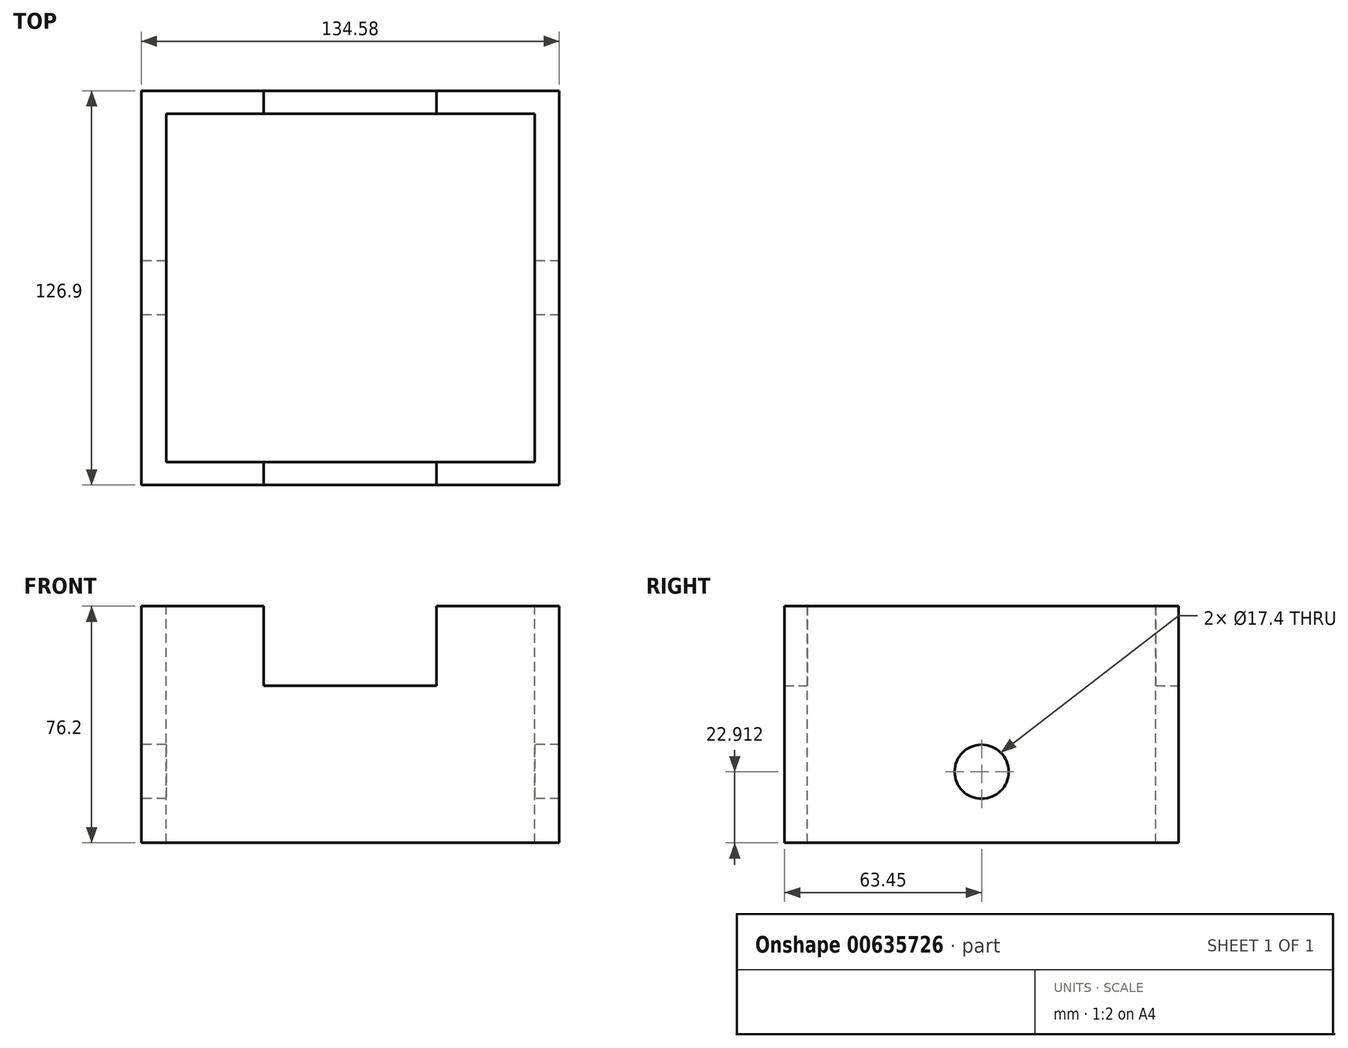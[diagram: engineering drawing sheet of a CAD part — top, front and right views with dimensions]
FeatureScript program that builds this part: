
annotation { "Feature Type Name" : "Feature", "Feature Type Description" : "" }
export const myFeature = defineFeature(function(context is Context, id is Id, definition is map)
    precondition{}
    {
        {
            var Q0;
            Q0=qCreatedBy(makeId("Top.planeOp"),FACE);
            var sketch = newSketch(context, id + "F0", { "sketchPlane" : qUnion([Q0])});
            skLineSegment(sketch, "E0.bottom", {"start": v(-67.29, 63.45) * mm, "end": v(67.29, 63.45) * mm});
            skLineSegment(sketch, "E0.top", {"start": v(-67.29, -63.45) * mm, "end": v(67.29, -63.45) * mm});
            skLineSegment(sketch, "E0.left", {"start": v(-67.29, 63.45) * mm, "end": v(-67.29, -63.45) * mm});
            skLineSegment(sketch, "E0.right", {"start": v(67.29, 63.45) * mm, "end": v(67.29, -63.45) * mm});
            skPoint(sketch, "E0.middle", {"position": v(0, 0) * mm});
            skLineSegment(sketch, "E1.bottom", {"start": v(-60.06, 53.2) * mm, "end": v(60.06, 53.2) * mm});
            skLineSegment(sketch, "E1.top", {"start": v(-60.06, -53.2) * mm, "end": v(60.06, -53.2) * mm});
            skLineSegment(sketch, "E1.left", {"start": v(-60.06, 53.2) * mm, "end": v(-60.06, -53.2) * mm});
            skLineSegment(sketch, "E1.right", {"start": v(60.06, 53.2) * mm, "end": v(60.06, -53.2) * mm});
            skSolve(sketch);
        }
        {
            var Q0;
            Q0=makeQuery(id+"F0.imprint","IMPRINT",FACE,{"disambiguationData":[TD([[makeQuery(id+"F0.imprint","IMPRINT",EDGE,{"derivedFrom":sQuery(id+"F0.wireOp",EDGE,"E1.bottom")}),-1.0]])]});
            var Q1;
            Q1=makeQuery(id+"F0.imprint","IMPRINT",FACE,{"disambiguationData":[TD([[makeQuery(id+"F0.imprint","IMPRINT",EDGE,{"derivedFrom":sQuery(id+"F0.wireOp",EDGE,"E0.bottom")}),-1.0]])]});
            extrude(context, id + "F1", {"entities" : qUnion([Q0, Q1]), "depth" : 50.8 * mm, "offsetDistance" : 25.4 * mm});
        }
        {
            var Q0;
            Q0=makeQuery(id+"F1.opExtrude","SWEPT_FACE",FACE,{"disambiguationData":[OSD([sQuery(id+"F0.wireOp",EDGE,"E0.left")])]});
            var sketch = newSketch(context, id + "F2", { "sketchPlane" : qUnion([Q0])});
            skCircle(sketch, "E2", {"center": v(0, 22.91) * mm, "radius": 8.7 * mm});
            skSolve(sketch);
        }
        {
            var Q0;
            Q0=makeQuery(id+"F2.imprint","IMPRINT",FACE,{"disambiguationData":[TD([[makeQuery(id+"F2.imprint","IMPRINT",EDGE,{"derivedFrom":sQuery(id+"F2.wireOp",EDGE,"E2")}),1.0]])]});
            extrude(context, id + "F3", {"entities" : qUnion([Q0]), "operationType" : NewBodyOperationType.REMOVE, "oppositeDirection" : true, "depth" : 508 * mm, "offsetDistance" : 25.4 * mm});
        }
        {
            var Q0;
            Q0=makeQuery(id+"F1.opExtrude","CAP_FACE",FACE,{"disambiguationData":[OSD([sQuery(id+"F0.wireOp",EDGE,"E0.bottom"),sQuery(id+"F0.wireOp",EDGE,"E0.top"),sQuery(id+"F0.wireOp",EDGE,"E0.left"),sQuery(id+"F0.wireOp",EDGE,"E0.right")])],"isStart":false});
            extrude(context, id + "F4", {"entities" : qUnion([Q0]), "operationType" : NewBodyOperationType.ADD, "depth" : 25.4 * mm, "offsetDistance" : 25.4 * mm});
        }
        {
            var Q0;
            Q0=makeQuery(id+"F4.opExtrude","CAP_FACE",FACE,{"disambiguationData":[OSD([sQuery(id+"F0.wireOp",EDGE,"E0.bottom"),sQuery(id+"F0.wireOp",EDGE,"E0.top"),sQuery(id+"F0.wireOp",EDGE,"E0.left"),sQuery(id+"F0.wireOp",EDGE,"E0.right")])],"isStart":false});
            var sketch = newSketch(context, id + "F5", { "sketchPlane" : qUnion([Q0])});
            skLineSegment(sketch, "E3.bottom", {"start": v(-59.3, 56.09) * mm, "end": v(59.3, 56.09) * mm});
            skLineSegment(sketch, "E3.top", {"start": v(-59.3, -56.09) * mm, "end": v(59.3, -56.09) * mm});
            skLineSegment(sketch, "E3.left", {"start": v(-59.3, 56.09) * mm, "end": v(-59.3, -56.09) * mm});
            skLineSegment(sketch, "E3.right", {"start": v(59.3, 56.09) * mm, "end": v(59.3, -56.09) * mm});
            skPoint(sketch, "E3.middle", {"position": v(0, 0) * mm});
            skSolve(sketch);
        }
        {
            var Q0;
            {var subQ0=sQuery(id+"F0.wireOp",EDGE,"E0.bottom");Q0=makeQuery(id+"F4.boolean.opBoolean","MERGE",FACE,{"derivedFrom":[makeQuery(id+"F1.opExtrude","SWEPT_FACE",FACE,{"disambiguationData":[OSD([subQ0])]}),makeQuery(id+"F4.opExtrude","SWEPT_FACE",FACE,{"disambiguationData":[OSD([subQ0])]})]});}
            var sketch = newSketch(context, id + "F6", { "sketchPlane" : qUnion([Q0])});
            skLineSegment(sketch, "E4.bottom", {"start": v(-27.77, 76.2) * mm, "end": v(27.95, 76.2) * mm});
            skLineSegment(sketch, "E4.top", {"start": v(-27.77, 50.6) * mm, "end": v(27.95, 50.6) * mm});
            skLineSegment(sketch, "E4.left", {"start": v(-27.77, 76.2) * mm, "end": v(-27.77, 50.6) * mm});
            skLineSegment(sketch, "E4.right", {"start": v(27.95, 76.2) * mm, "end": v(27.95, 50.6) * mm});
            skSolve(sketch);
        }
        {
            var Q0;
            Q0=makeQuery(id+"F6.imprint","IMPRINT",FACE,{"disambiguationData":[TD([[makeQuery(id+"F6.imprint","IMPRINT",EDGE,{"derivedFrom":sQuery(id+"F6.wireOp",EDGE,"E4.bottom")}),1.0]])]});
            extrude(context, id + "F7", {"entities" : qUnion([Q0]), "operationType" : NewBodyOperationType.REMOVE, "oppositeDirection" : true, "depth" : 584.2 * mm, "offsetDistance" : 25.4 * mm});
        }
        {
            var Q0;
            Q0=makeQuery(id+"F5.imprint","IMPRINT",FACE,{"disambiguationData":[TD([[makeQuery(id+"F5.imprint","IMPRINT",EDGE,{"derivedFrom":sQuery(id+"F5.wireOp",EDGE,"E3.bottom")}),-1.0]])]});
            extrude(context, id + "F8", {"entities" : qUnion([Q0]), "operationType" : NewBodyOperationType.REMOVE, "oppositeDirection" : true, "depth" : 508 * mm, "offsetDistance" : 25.4 * mm});
        }
    });
